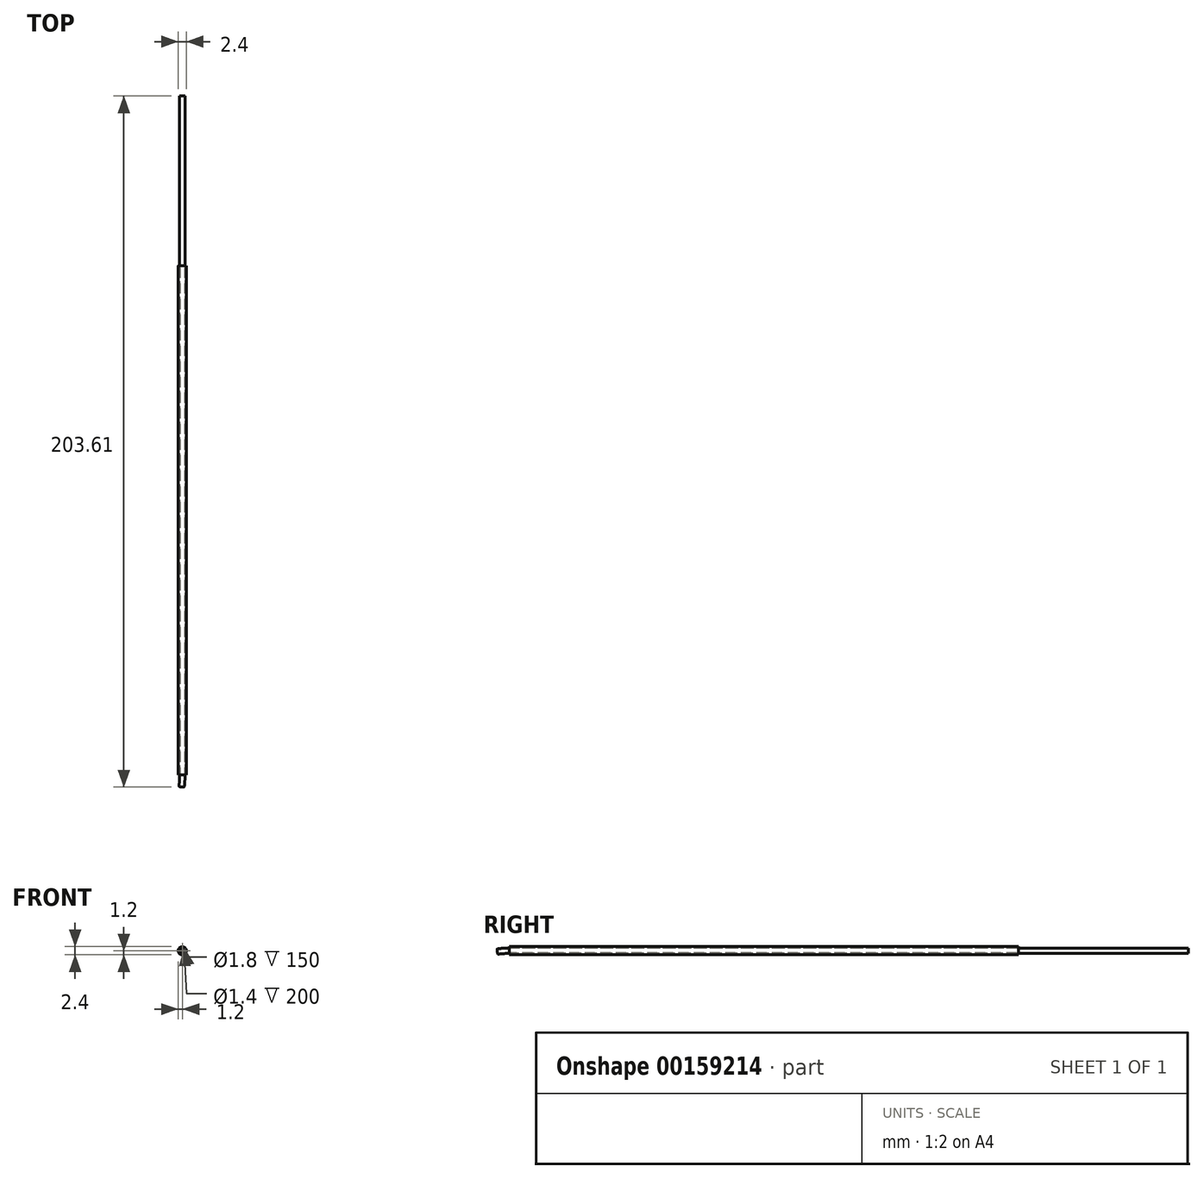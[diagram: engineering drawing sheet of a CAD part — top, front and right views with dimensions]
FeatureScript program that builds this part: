
annotation { "Feature Type Name" : "Feature", "Feature Type Description" : "" }
export const myFeature = defineFeature(function(context is Context, id is Id, definition is map)
    precondition{}
    {
        {
            assignVariable(context, id + "F0", {"name" : "TubeTransmissionLength", "anyValue" : 200});
        }
        {
            var Q0;
            Q0=qCreatedBy(makeId("Front.planeOp"),FACE);
            var sketch = newSketch(context, id + "F1", { "sketchPlane" : qUnion([Q0])});
            skCircle(sketch, "E0", {"center": v(0, 0) * mm, "radius": 0.7 * mm});
            skCircle(sketch, "E1", {"center": v(0, 0) * mm, "radius": 0.8 * mm});
            skSolve(sketch);
        }
        {
            var Q0;
            Q0=qCreatedBy(makeId("Top.planeOp"),FACE);
            var sketch = newSketch(context, id + "F2", { "sketchPlane" : qUnion([Q0])});
            skLineSegment(sketch, "E2", {"start": v(0, 0) * mm, "end": v(0, -200) * mm});
            skLineSegment(sketch, "E3", {"start": v(0, -145.32) * mm, "end": v(0, -200) * mm, "construction": true});
            skLineSegment(sketch, "E4", {"start": v(0, -200) * mm, "end": v(-20, -200) * mm, "construction": true});
            skArc(sketch, "E5", {"start": v(0, -200) * mm, "mid": v(-0.08, -201.74) * mm, "end": v(-0.3, -203.47) * mm});
            skLineSegment(sketch, "E6", {"start": v(-0.3, -203.47) * mm, "end": v(-0.3, -203.47) * mm});
            skSolve(sketch);
        }
        {
            var Q0;
            Q0=makeQuery(id+"F1.imprint","IMPRINT",FACE,{"disambiguationData":[TD([[makeQuery(id+"F1.imprint","IMPRINT",EDGE,{"derivedFrom":sQuery(id+"F1.wireOp",EDGE,"E0")}),-1.0]])]});
            var Q1;
            Q1=sQuery(id+"F2.wireOp",EDGE,"E2");
            var Q2;
            Q2=sQuery(id+"F2.wireOp",EDGE,"E5");
            var Q3;
            Q3=sQuery(id+"F2.wireOp",EDGE,"E6");
            sweep(context, id + "F3", {"profiles" : qUnion([Q0]), "path" : qUnion([Q1, Q2, Q3])});
        }
        {
            var Q0;
            Q0=makeQuery(id+"F3.opSweep","CAP_FACE",FACE,{"disambiguationData":[OSD([sQuery(id+"F1.wireOp",EDGE,"E0"),sQuery(id+"F1.wireOp",EDGE,"E1"),sQuery(id+"F2.wireOp",VERTEX,"E2.start")])],"isStart":true});
            cPlane(context, id + "F4", {"entities" : qUnion([Q0]), "cplaneType" : CPlaneType.OFFSET, "offset" : 50 * mm, "oppositeDirection" : true, "width" : 150 * mm, "height" : 150 * mm});
        }
        {
            var Q0;
            Q0=qCreatedBy(id+"F4.planeOp",FACE);
            var sketch = newSketch(context, id + "F5", { "sketchPlane" : qUnion([Q0])});
            skCircle(sketch, "E7.0", {"center": v(0, 0) * mm, "radius": 0.8 * mm});
            skCircle(sketch, "E7.1", {"center": v(0, 0) * mm, "radius": 0.7 * mm});
            skCircle(sketch, "E8", {"center": v(0, 0) * mm, "radius": 0.9 * mm});
            skCircle(sketch, "E9", {"center": v(0, 0) * mm, "radius": 1.2 * mm});
            skSolve(sketch);
        }
        {
            var Q0;
            Q0=makeQuery(id+"F5.imprint","IMPRINT",FACE,{"disambiguationData":[TD([[makeQuery(id+"F5.imprint","IMPRINT",EDGE,{"derivedFrom":sQuery(id+"F5.wireOp",EDGE,"E8")}),-1.0]])]});
            var Q1;
            Q1=makeQuery(id+"F3.opSweep","SWEPT_FACE",FACE,{"disambiguationData":[OSD([sQuery(id+"F1.wireOp",EDGE,"E1"),sQuery(id+"F2.wireOp",EDGE,"E2")])]});
            extrude(context, id + "F6", {"entities" : qUnion([Q0]), "oppositeDirection" : true, "endBoundEntityFace" : qUnion([Q1]), "depth" : (getVariable(context, 'TubeTransmissionLength') - 50) * mm});
        }
        {
            var Q0;
            Q0=makeQuery(id+"F6.opExtrude","CAP_FACE",FACE,{"disambiguationData":[OSD([sQuery(id+"F5.wireOp",EDGE,"E8"),sQuery(id+"F5.wireOp",EDGE,"E9")])],"isStart":true});
            cPlane(context, id + "F7", {"entities" : qUnion([Q0]), "cplaneType" : CPlaneType.OFFSET, "offset" : 50 * mm, "oppositeDirection" : true, "width" : 150 * mm, "height" : 150 * mm});
        }
        {
            var Q0;
            Q0=qCreatedBy(id+"F7.planeOp",FACE);
            var sketch = newSketch(context, id + "F8", { "sketchPlane" : qUnion([Q0])});
            skCircle(sketch, "E10.0", {"center": v(0, 0) * mm, "radius": 1.2 * mm});
            skLineSegment(sketch, "E11", {"start": v(0, 0) * mm, "end": v(0, 9.07) * mm});
            skLineSegment(sketch, "E12", {"start": v(0, 0) * mm, "end": v(-8.67, 0) * mm});
            skSolve(sketch);
        }
        {
            var Q0;
            Q0=makeQuery(id+"F6.opExtrude","SWEPT_BODY",BODY,{"disambiguationData":[OSD([sQuery(id+"F5.wireOp",EDGE,"E8"),sQuery(id+"F5.wireOp",EDGE,"E9")])]});
            var Q1;
            Q1=makeQuery(id+"F3.opSweep","SWEPT_BODY",BODY,{"disambiguationData":[OSD([sQuery(id+"F1.wireOp",EDGE,"E0"),sQuery(id+"F1.wireOp",EDGE,"E1"),sQuery(id+"F2.wireOp",EDGE,"E5")])]});
            transform(context, id + "F9", {"entities" : qUnion([Q0, Q1]), "transformType" : TransformType.TRANSLATION_3D, "dx" : 0 * mm, "dy" : 5.5 * mm, "dz" : 0 * mm, "makeCopy" : false});
        }
        {
            var Q0;
            Q0=makeQuery(id+"F6.opExtrude","SWEPT_BODY",BODY,{"disambiguationData":[OSD([sQuery(id+"F5.wireOp",EDGE,"E8"),sQuery(id+"F5.wireOp",EDGE,"E9")])]});
            var Q1;
            Q1=makeQuery(id+"F3.opSweep","SWEPT_BODY",BODY,{"disambiguationData":[OSD([sQuery(id+"F1.wireOp",EDGE,"E0"),sQuery(id+"F1.wireOp",EDGE,"E1"),sQuery(id+"F2.wireOp",EDGE,"E5")])]});
            var Q2;
            Q2=sQuery(id+"F2.wireOp",EDGE,"E2");
            transform(context, id + "F10", {"entities" : qUnion([Q0, Q1]), "transformType" : TransformType.ROTATION, "transformAxis" : qUnion([Q2]), "angle" : 50 * degree, "makeCopy" : false});
        }
    });
